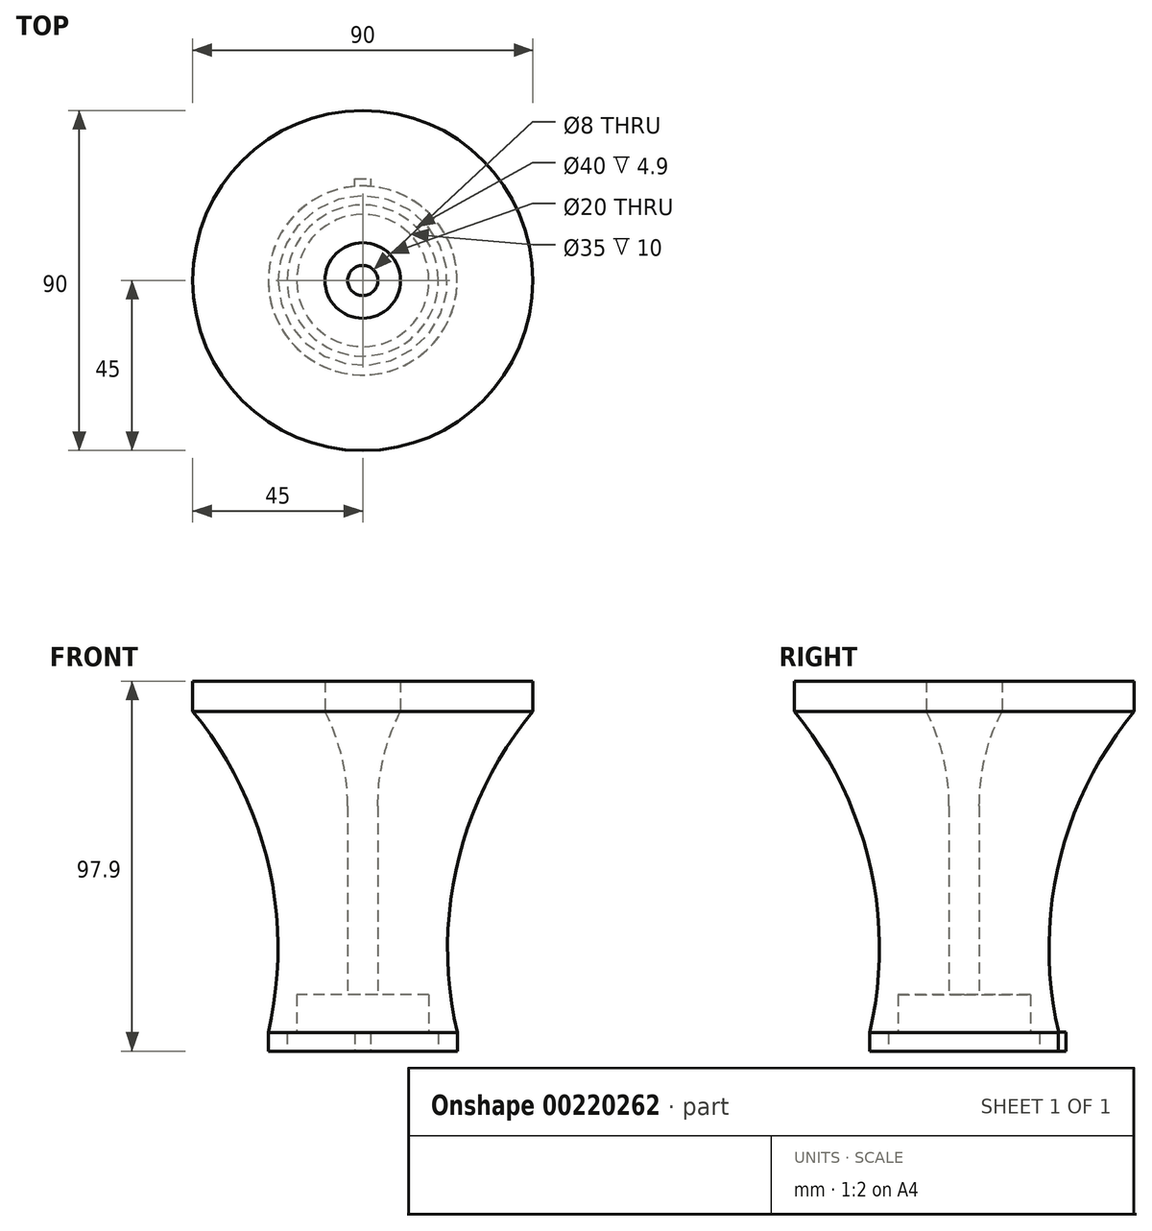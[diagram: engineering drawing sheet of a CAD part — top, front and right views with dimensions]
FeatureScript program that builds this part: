
annotation { "Feature Type Name" : "Feature", "Feature Type Description" : "" }
export const myFeature = defineFeature(function(context is Context, id is Id, definition is map)
    precondition{}
    {
        {
            var Q0;
            Q0=qCreatedBy(makeId("Front.planeOp"),FACE);
            var sketch = newSketch(context, id + "F0", { "sketchPlane" : qUnion([Q0])});
            skLineSegment(sketch, "E0", {"start": v(25, 0) * mm, "end": v(4, 0) * mm});
            skLineSegment(sketch, "E1", {"start": v(4, 0) * mm, "end": v(4, 60) * mm});
            skLineSegment(sketch, "E2", {"start": v(10, 85) * mm, "end": v(45, 85) * mm});
            skArc(sketch, "E3", {"start": v(45, 85) * mm, "mid": v(25.06, 44.84) * mm, "end": v(25, 0) * mm});
            skArc(sketch, "E4", {"start": v(10, 85) * mm, "mid": v(5.52, 72.85) * mm, "end": v(4, 60) * mm});
            skSolve(sketch);
        }
        {
            var Q0;
            Q0=qCreatedBy(makeId("Front.planeOp"),FACE);
            var sketch = newSketch(context, id + "F1", { "sketchPlane" : qUnion([Q0])});
            skLineSegment(sketch, "E5", {"start": v(0, 0) * mm, "end": v(0, 50.34) * mm});
            skSolve(sketch);
        }
        {
            var Q0;
            Q0=makeQuery(id+"F0.imprint","IMPRINT",FACE,{"disambiguationData":[TD([[makeQuery(id+"F0.imprint","IMPRINT",EDGE,{"derivedFrom":sQuery(id+"F0.wireOp",EDGE,"E0")}),-1.0]])]});
            var Q1;
            Q1=sQuery(id+"F1.wireOp",EDGE,"E5");
            revolve(context, id + "F2", {"entities" : qUnion([Q0]), "axis" : qUnion([Q1]), "revolveType" : RevolveType.FULL});
        }
        {
            var Q0;
            Q0=makeQuery(id+"F2.opRevolve","SWEPT_FACE",FACE,{"disambiguationData":[OSD([sQuery(id+"F0.wireOp",EDGE,"E0")])]});
            extrude(context, id + "F3", {"entities" : qUnion([Q0]), "operationType" : NewBodyOperationType.ADD, "depth" : 4.9 * mm});
        }
        {
            var Q0;
            Q0=makeQuery(id+"F3.opExtrude","CAP_FACE",FACE,{"disambiguationData":[OSD([sQuery(id+"F0.wireOp",EDGE,"E0")])],"isStart":false});
            var sketch = newSketch(context, id + "F4", { "sketchPlane" : qUnion([Q0])});
            skCircle(sketch, "E6", {"center": v(0, 0) * mm, "radius": 20 * mm});
            skSolve(sketch);
        }
        {
            var Q0;
            Q0=makeQuery(id+"F4.imprint","IMPRINT",FACE,{"disambiguationData":[TD([[makeQuery(id+"F4.imprint","IMPRINT",EDGE,{"derivedFrom":sQuery(id+"F4.wireOp",EDGE,"E6")}),1.0]])]});
            var Q1;
            Q1=sQuery(id+"F4.wireOp",EDGE,"E6");
            extrude(context, id + "F5", {"entities" : qUnion([Q0]), "operationType" : NewBodyOperationType.REMOVE, "surfaceEntities" : qUnion([Q1]), "oppositeDirection" : true, "depth" : 4.9 * mm});
        }
        {
            var Q0;
            Q0=makeQuery(id+"F2.opRevolve","SWEPT_FACE",FACE,{"disambiguationData":[OSD([sQuery(id+"F0.wireOp",EDGE,"E2")])]});
            extrude(context, id + "F6", {"entities" : qUnion([Q0]), "operationType" : NewBodyOperationType.ADD, "depth" : 8 * mm});
        }
        {
            var Q0;
            Q0=qCreatedBy(makeId("Top.planeOp"),FACE);
            var sketch = newSketch(context, id + "F7", { "sketchPlane" : qUnion([Q0])});
            skCircle(sketch, "E7", {"center": v(0, 0) * mm, "radius": 17.5 * mm});
            skSolve(sketch);
        }
        {
            var Q0;
            Q0=qSketchRegion(id+"F7",true);
            extrude(context, id + "F8", {"entities" : qUnion([Q0]), "operationType" : NewBodyOperationType.REMOVE, "depth" : 10 * mm});
        }
        {
            var Q0;
            Q0=makeQuery(id+"F4.imprint","IMPRINT",FACE,{"disambiguationData":[TD([[makeQuery(id+"F4.imprint","IMPRINT",EDGE,{"derivedFrom":sQuery(id+"F4.wireOp",EDGE,"E6")}),-1.0]])]});
            var sketch = newSketch(context, id + "F9", { "sketchPlane" : qUnion([Q0])});
            skArc(sketch, "E8", {"start": v(-2.12, -24.9) * mm, "mid": v(0, -25) * mm, "end": v(2.13, -24.9) * mm});
            skLineSegment(sketch, "E9", {"start": v(0, 0) * mm, "end": v(0, -36.79) * mm, "construction": true});
            skLineSegment(sketch, "E10", {"start": v(-2.12, -24.9) * mm, "end": v(-2.12, -26.9) * mm});
            skLineSegment(sketch, "E11", {"start": v(-2.12, -26.9) * mm, "end": v(2.13, -26.9) * mm});
            skLineSegment(sketch, "E12", {"start": v(2.13, -26.9) * mm, "end": v(2.13, -24.9) * mm});
            skSolve(sketch);
        }
        {
            var Q0;
            Q0=qSketchRegion(id+"F9",true);
            extrude(context, id + "F10", {"entities" : qUnion([Q0]), "operationType" : NewBodyOperationType.ADD, "oppositeDirection" : true, "depth" : 5 * mm});
        }
    });
